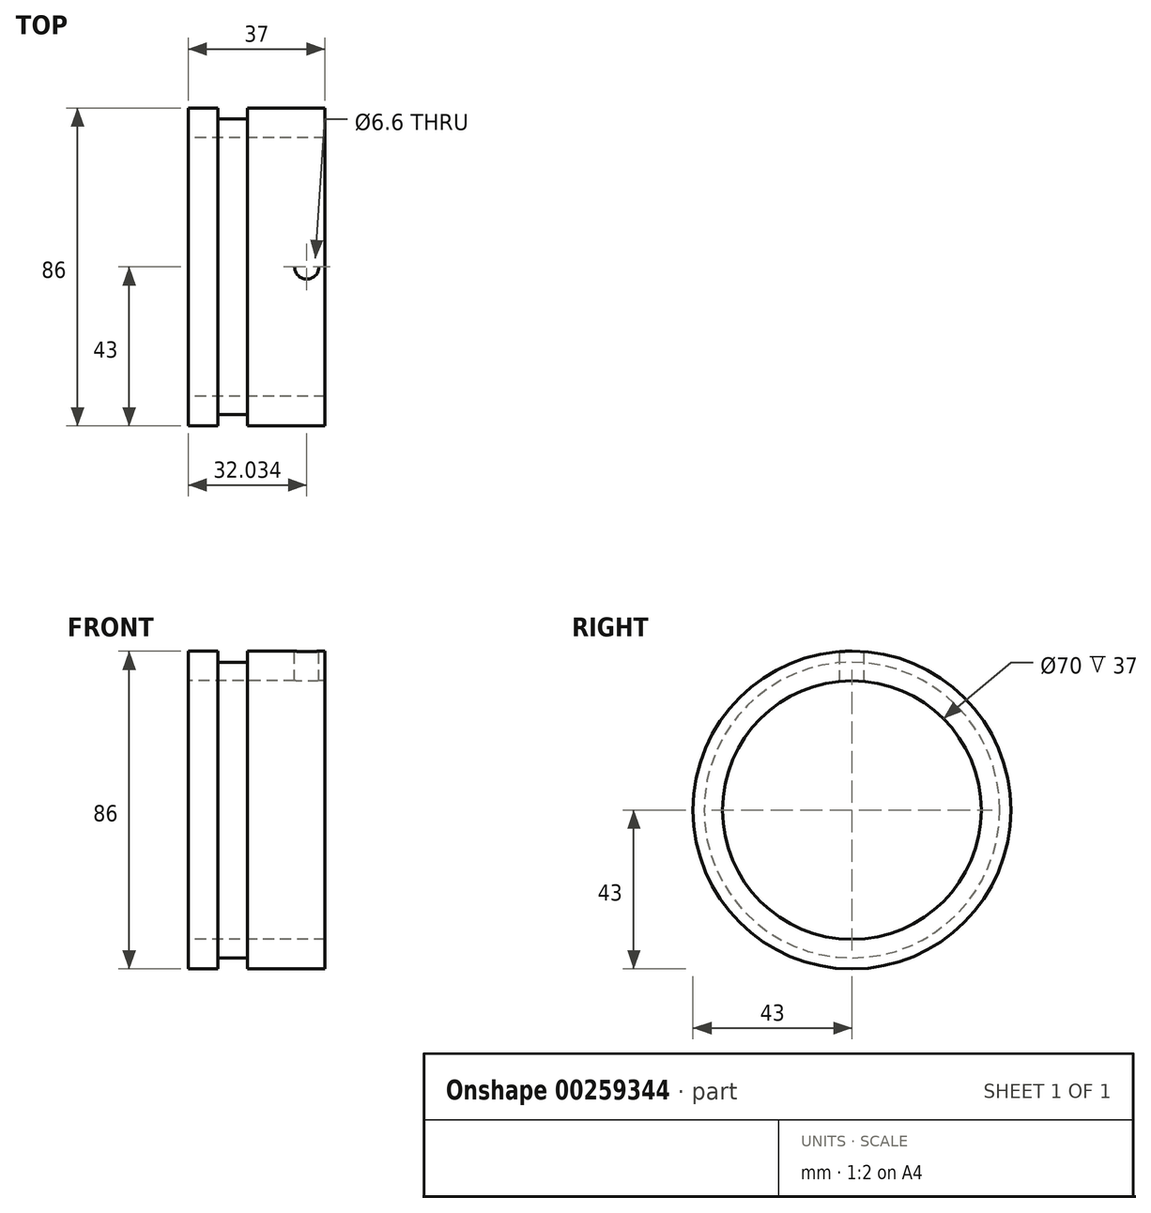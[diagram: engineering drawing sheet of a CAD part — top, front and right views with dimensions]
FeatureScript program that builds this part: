
annotation { "Feature Type Name" : "Feature", "Feature Type Description" : "" }
export const myFeature = defineFeature(function(context is Context, id is Id, definition is map)
    precondition{}
    {
        {
            var Q0;
            Q0=qCreatedBy(makeId("Front.planeOp"),FACE);
            var sketch = newSketch(context, id + "F0", { "sketchPlane" : qUnion([Q0])});
            skLineSegment(sketch, "E0", {"start": v(0, 0) * mm, "end": v(24.6, 0) * mm, "construction": true});
            skLineSegment(sketch, "E1", {"start": v(0, 35) * mm, "end": v(0, 43) * mm});
            skLineSegment(sketch, "E2", {"start": v(0, 43) * mm, "end": v(8, 43) * mm});
            skLineSegment(sketch, "E3", {"start": v(8, 43) * mm, "end": v(8, 40) * mm});
            skLineSegment(sketch, "E4", {"start": v(8, 40) * mm, "end": v(16, 40) * mm});
            skLineSegment(sketch, "E5", {"start": v(16, 40) * mm, "end": v(16, 43) * mm});
            skLineSegment(sketch, "E6", {"start": v(16, 43) * mm, "end": v(37, 43) * mm});
            skLineSegment(sketch, "E7", {"start": v(0, 35) * mm, "end": v(37, 35) * mm});
            skLineSegment(sketch, "E8", {"start": v(37, 43) * mm, "end": v(37, 35) * mm});
            skLineSegment(sketch, "E9", {"start": v(12, 40) * mm, "end": v(12, 54.35) * mm, "construction": true});
            skSolve(sketch);
        }
        {
            var Q0;
            Q0=makeQuery(id+"F0.imprint","IMPRINT",FACE,{"disambiguationData":[TD([[makeQuery(id+"F0.imprint","IMPRINT",EDGE,{"derivedFrom":sQuery(id+"F0.wireOp",EDGE,"E1")}),-1.0]])]});
            var Q1;
            Q1=sQuery(id+"F0.wireOp",EDGE,"E0");
            revolve(context, id + "F1", {"entities" : qUnion([Q0]), "axis" : qUnion([Q1]), "revolveType" : RevolveType.FULL});
        }
        {
            var Q0;
            Q0=qCreatedBy(makeId("Right.planeOp"),FACE);
            cPlane(context, id + "F2", {"entities" : qUnion([Q0]), "cplaneType" : CPlaneType.OFFSET, "offset" : 37 * mm, "width" : 150 * mm, "height" : 150 * mm});
        }
        {
            var Q0;
            Q0=qCreatedBy(makeId("Top.planeOp"),FACE);
            cPlane(context, id + "F3", {"entities" : qUnion([Q0]), "cplaneType" : CPlaneType.OFFSET, "offset" : 43 * mm, "width" : 150 * mm, "height" : 150 * mm});
        }
        {
            var Q0;
            Q0=qCreatedBy(id+"F3.planeOp",FACE);
            var sketch = newSketch(context, id + "F4", { "sketchPlane" : qUnion([Q0])});
            skCircle(sketch, "E10", {"center": v(32.03, 0) * mm, "radius": 17.32 * mm, "construction": true});
            skLineSegment(sketch, "E11", {"start": v(32.03, 0) * mm, "end": v(32.03, -10.42) * mm, "construction": true});
            skLineSegment(sketch, "E12", {"start": v(32.03, 0) * mm, "end": v(42.08, 0) * mm, "construction": true});
            skSolve(sketch);
        }
        {
            var Q0;
            Q0=sQuery(id+"F4.wireOp",VERTEX,"E10.center");
            var Q1;
            Q1=makeQuery(id+"F1.opRevolve","SWEPT_BODY",BODY,{"disambiguationData":[OSD([sQuery(id+"F0.wireOp",EDGE,"E1"),sQuery(id+"F0.wireOp",EDGE,"E2"),sQuery(id+"F0.wireOp",EDGE,"E3"),sQuery(id+"F0.wireOp",EDGE,"E4"),sQuery(id+"F0.wireOp",EDGE,"E5"),sQuery(id+"F0.wireOp",EDGE,"E6"),sQuery(id+"F0.wireOp",EDGE,"E7"),sQuery(id+"F0.wireOp",EDGE,"E8")])]});
            hole(context, id + "F5", {"style" : HoleStyle.SIMPLE, "endStyle" : HoleEndStyle.BLIND, "standardTappedOrClearance" : lookupTablePath({ "standard" : "ISO", "fit" : "Normal", "size" : "M6", "type" : "Clearance" }), "standardBlindInLast" : lookupTablePath({ "fit" : "Standard", "standard" : "ISO", "size" : "M6", "type" : "Clearance" }), "holeDiameter" : 6.6 * mm, "holeDepth" : 15 * mm, "tappedDepth" : 12 * mm, "tapClearance" : 3, "locations" : qUnion([Q0]), "scope" : qUnion([Q1])});
        }
    });
